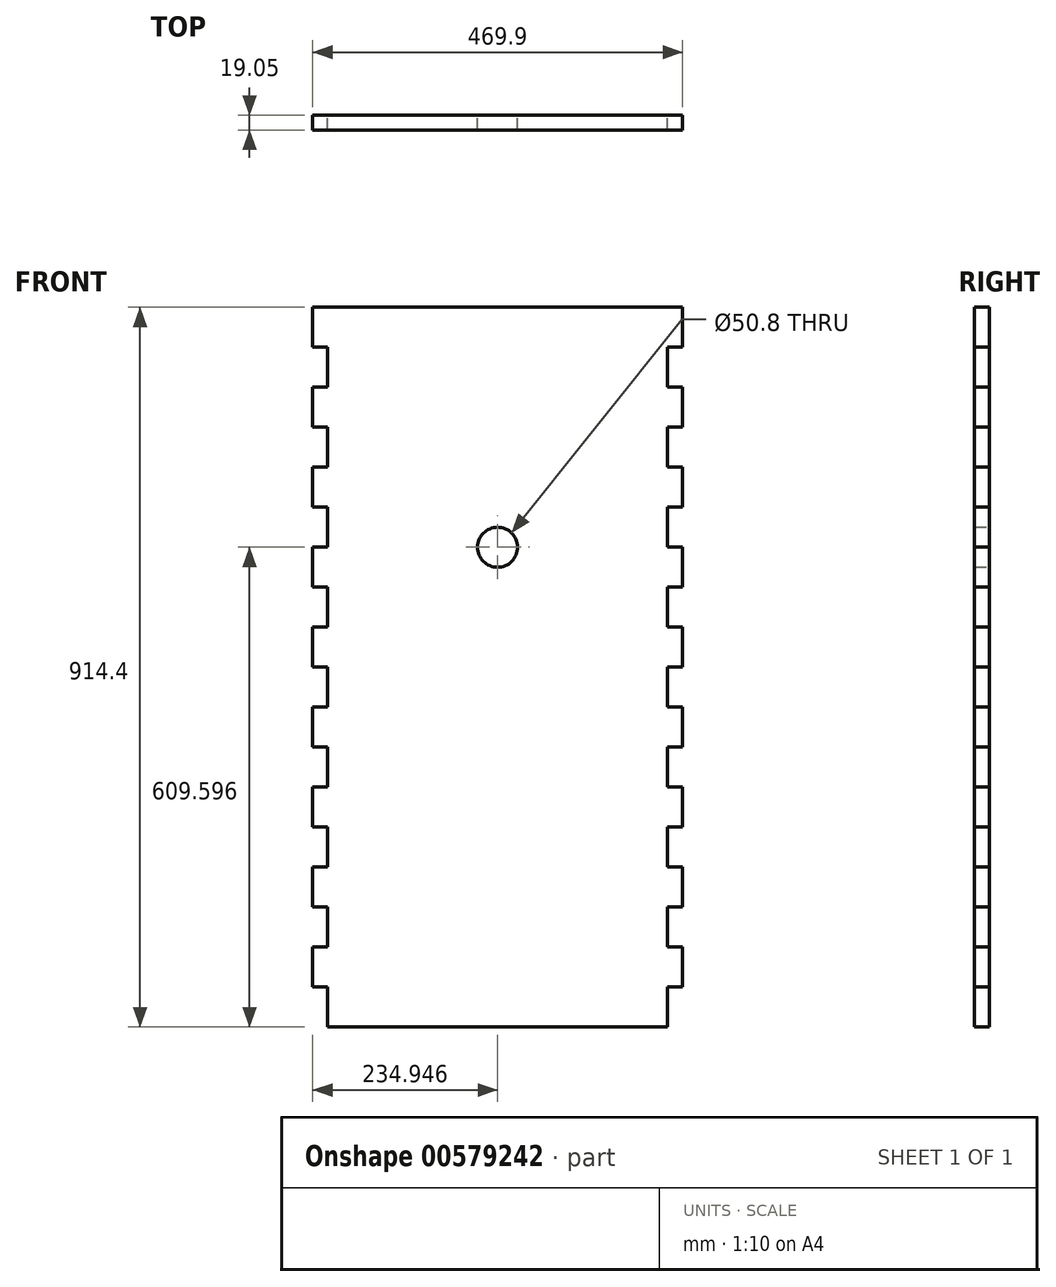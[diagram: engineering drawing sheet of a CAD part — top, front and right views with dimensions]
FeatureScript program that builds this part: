
annotation { "Feature Type Name" : "Feature", "Feature Type Description" : "" }
export const myFeature = defineFeature(function(context is Context, id is Id, definition is map)
    precondition{}
    {
        {
            var Q0;
            Q0=qCreatedBy(makeId("Front.planeOp"),FACE);
            var sketch = newSketch(context, id + "F0", { "sketchPlane" : qUnion([Q0])});
            skLineSegment(sketch, "E0.top", {"start": v(-296.68, -96.4) * mm, "end": v(135.12, -96.4) * mm});
            skLineSegment(sketch, "E0.left", {"start": v(-315.73, 106.8) * mm, "end": v(-315.73, 56) * mm});
            skLineSegment(sketch, "E0.right", {"start": v(154.17, 106.8) * mm, "end": v(154.17, 56) * mm});
            skLineSegment(sketch, "E1.bottom", {"start": v(135.12, -45.6) * mm, "end": v(154.17, -45.6) * mm});
            skLineSegment(sketch, "E1.left", {"start": v(135.12, -45.6) * mm, "end": v(135.12, -96.4) * mm});
            skLineSegment(sketch, "E2.top", {"start": v(-315.73, 106.8) * mm, "end": v(-296.68, 106.8) * mm});
            skLineSegment(sketch, "E3.bottom", {"start": v(-315.73, 56) * mm, "end": v(-296.68, 56) * mm});
            skLineSegment(sketch, "E3.top", {"start": v(-315.73, 5.2) * mm, "end": v(-296.68, 5.2) * mm});
            skLineSegment(sketch, "E3.right", {"start": v(-296.68, 56) * mm, "end": v(-296.68, 5.2) * mm});
            skLineSegment(sketch, "E4.top", {"start": v(-315.73, -45.6) * mm, "end": v(-296.68, -45.6) * mm});
            skLineSegment(sketch, "E4.left", {"start": v(-315.73, 5.2) * mm, "end": v(-315.73, -45.6) * mm});
            skLineSegment(sketch, "E5.right", {"start": v(-296.68, -45.6) * mm, "end": v(-296.68, -96.4) * mm});
            skLineSegment(sketch, "E6.bottom", {"start": v(135.12, 5.2) * mm, "end": v(154.17, 5.2) * mm});
            skLineSegment(sketch, "E6.right", {"start": v(154.17, 5.2) * mm, "end": v(154.17, -45.6) * mm});
            skLineSegment(sketch, "E7.bottom", {"start": v(135.12, 56) * mm, "end": v(154.17, 56) * mm});
            skLineSegment(sketch, "E7.left", {"start": v(135.12, 56) * mm, "end": v(135.12, 5.2) * mm});
            skLineSegment(sketch, "E8.top", {"start": v(135.12, 106.8) * mm, "end": v(154.17, 106.8) * mm});
            skLineSegment(sketch, "E9.bottom", {"start": v(-315.73, 310) * mm, "end": v(-296.68, 310) * mm});
            skLineSegment(sketch, "E9.top", {"start": v(-315.73, 360.8) * mm, "end": v(-296.68, 360.8) * mm});
            skLineSegment(sketch, "E9.right", {"start": v(-296.68, 310) * mm, "end": v(-296.68, 360.8) * mm});
            skLineSegment(sketch, "E10.bottom", {"start": v(-315.73, 208.4) * mm, "end": v(-296.68, 208.4) * mm});
            skLineSegment(sketch, "E10.top", {"start": v(-315.73, 259.2) * mm, "end": v(-296.68, 259.2) * mm});
            skLineSegment(sketch, "E10.right", {"start": v(-296.68, 208.4) * mm, "end": v(-296.68, 259.2) * mm});
            skLineSegment(sketch, "E11.bottom", {"start": v(-315.73, 157.6) * mm, "end": v(-296.68, 157.6) * mm});
            skLineSegment(sketch, "E11.left", {"start": v(-315.73, 157.6) * mm, "end": v(-315.73, 208.4) * mm});
            skLineSegment(sketch, "E12.left", {"start": v(-315.73, 259.2) * mm, "end": v(-315.73, 310) * mm});
            skLineSegment(sketch, "E13.right", {"start": v(-296.68, 106.8) * mm, "end": v(-296.68, 157.6) * mm});
            skLineSegment(sketch, "E14.top", {"start": v(-315.73, 411.6) * mm, "end": v(-296.68, 411.6) * mm});
            skLineSegment(sketch, "E14.left", {"start": v(-315.73, 360.8) * mm, "end": v(-315.73, 411.6) * mm});
            skLineSegment(sketch, "E15.top", {"start": v(-315.73, 462.4) * mm, "end": v(-296.68, 462.4) * mm});
            skLineSegment(sketch, "E15.right", {"start": v(-296.68, 411.6) * mm, "end": v(-296.68, 462.4) * mm});
            skLineSegment(sketch, "E16.bottom", {"start": v(135.12, 360.8) * mm, "end": v(154.17, 360.8) * mm});
            skLineSegment(sketch, "E16.top", {"start": v(135.12, 411.6) * mm, "end": v(154.17, 411.6) * mm});
            skLineSegment(sketch, "E16.right", {"start": v(154.17, 360.8) * mm, "end": v(154.17, 411.6) * mm});
            skLineSegment(sketch, "E17.top", {"start": v(135.12, 462.4) * mm, "end": v(154.17, 462.4) * mm});
            skLineSegment(sketch, "E17.left", {"start": v(135.12, 411.6) * mm, "end": v(135.12, 462.4) * mm});
            skLineSegment(sketch, "E18.bottom", {"start": v(135.12, 259.2) * mm, "end": v(154.17, 259.2) * mm});
            skLineSegment(sketch, "E18.top", {"start": v(135.12, 310) * mm, "end": v(154.17, 310) * mm});
            skLineSegment(sketch, "E18.right", {"start": v(154.17, 259.2) * mm, "end": v(154.17, 310) * mm});
            skLineSegment(sketch, "E19.left", {"start": v(135.12, 310) * mm, "end": v(135.12, 360.8) * mm});
            skLineSegment(sketch, "E20.top", {"start": v(135.12, 157.6) * mm, "end": v(154.17, 157.6) * mm});
            skLineSegment(sketch, "E20.left", {"start": v(135.12, 106.8) * mm, "end": v(135.12, 157.6) * mm});
            skLineSegment(sketch, "E21.bottom", {"start": v(135.12, 208.4) * mm, "end": v(154.17, 208.4) * mm});
            skLineSegment(sketch, "E21.left", {"start": v(135.12, 208.4) * mm, "end": v(135.12, 259.2) * mm});
            skLineSegment(sketch, "E22.right", {"start": v(154.17, 157.6) * mm, "end": v(154.17, 208.4) * mm});
            skLineSegment(sketch, "E23.bottom", {"start": v(-315.73, 716.4) * mm, "end": v(-296.68, 716.4) * mm});
            skLineSegment(sketch, "E23.top", {"start": v(-315.73, 767.2) * mm, "end": v(-296.68, 767.2) * mm});
            skLineSegment(sketch, "E23.right", {"start": v(-296.68, 716.4) * mm, "end": v(-296.68, 767.2) * mm});
            skLineSegment(sketch, "E24.bottom", {"start": v(-315.73, 665.6) * mm, "end": v(-296.68, 665.6) * mm});
            skLineSegment(sketch, "E24.left", {"start": v(-315.73, 665.6) * mm, "end": v(-315.73, 716.4) * mm});
            skLineSegment(sketch, "E25.top", {"start": v(-315.73, 818) * mm, "end": v(-296.68, 818) * mm});
            skLineSegment(sketch, "E25.left", {"start": v(-315.73, 767.2) * mm, "end": v(-315.73, 818) * mm});
            skLineSegment(sketch, "E26.bottom", {"start": v(-315.73, 614.8) * mm, "end": v(-296.68, 614.8) * mm});
            skLineSegment(sketch, "E26.right", {"start": v(-296.68, 614.8) * mm, "end": v(-296.68, 665.6) * mm});
            skLineSegment(sketch, "E27.bottom", {"start": v(-315.73, 564) * mm, "end": v(-296.68, 564) * mm});
            skLineSegment(sketch, "E27.left", {"start": v(-315.73, 564) * mm, "end": v(-315.73, 614.8) * mm});
            skLineSegment(sketch, "E28.top", {"start": v(-315.73, 513.2) * mm, "end": v(-296.68, 513.2) * mm});
            skLineSegment(sketch, "E28.left", {"start": v(-315.73, 462.4) * mm, "end": v(-315.73, 513.2) * mm});
            skLineSegment(sketch, "E29.right", {"start": v(-296.68, 513.2) * mm, "end": v(-296.68, 564) * mm});
            skLineSegment(sketch, "E30.bottom", {"start": v(135.12, 513.2) * mm, "end": v(154.17, 513.2) * mm});
            skLineSegment(sketch, "E30.top", {"start": v(135.12, 564) * mm, "end": v(154.17, 564) * mm});
            skLineSegment(sketch, "E30.left", {"start": v(135.12, 513.2) * mm, "end": v(135.12, 564) * mm});
            skLineSegment(sketch, "E31.top", {"start": v(135.12, 614.8) * mm, "end": v(154.17, 614.8) * mm});
            skLineSegment(sketch, "E31.right", {"start": v(154.17, 564) * mm, "end": v(154.17, 614.8) * mm});
            skLineSegment(sketch, "E32.right", {"start": v(154.17, 462.4) * mm, "end": v(154.17, 513.2) * mm});
            skLineSegment(sketch, "E33.bottom", {"start": v(135.12, 665.6) * mm, "end": v(154.17, 665.6) * mm});
            skLineSegment(sketch, "E33.top", {"start": v(135.12, 716.4) * mm, "end": v(154.17, 716.4) * mm});
            skLineSegment(sketch, "E33.right", {"start": v(154.17, 665.6) * mm, "end": v(154.17, 716.4) * mm});
            skLineSegment(sketch, "E34.left", {"start": v(135.12, 614.8) * mm, "end": v(135.12, 665.6) * mm});
            skLineSegment(sketch, "E35.top", {"start": v(135.12, 767.2) * mm, "end": v(154.17, 767.2) * mm});
            skLineSegment(sketch, "E35.left", {"start": v(135.12, 716.4) * mm, "end": v(135.12, 767.2) * mm});
            skLineSegment(sketch, "E36.top", {"start": v(135.12, 818) * mm, "end": v(154.17, 818) * mm});
            skLineSegment(sketch, "E36.right", {"start": v(154.17, 767.2) * mm, "end": v(154.17, 818) * mm});
            skLineSegment(sketch, "E37", {"start": v(135.12, 818) * mm, "end": v(-296.68, 818) * mm});
            skCircle(sketch, "E38", {"center": v(-80.78, 513.2) * mm, "radius": 25.4 * mm});
            skSolve(sketch);
        }
        {
            var Q0;
            Q0=makeQuery(id+"F0.imprint","IMPRINT",FACE,{"disambiguationData":[TD([[makeQuery(id+"F0.imprint","IMPRINT",EDGE,{"derivedFrom":sQuery(id+"F0.wireOp",EDGE,"E0.top")}),1.0]])]});
            extrude(context, id + "F1", {"entities" : qUnion([Q0]), "depth" : 19.05 * mm, "offsetDistance" : 25.4 * mm});
        }
    });
